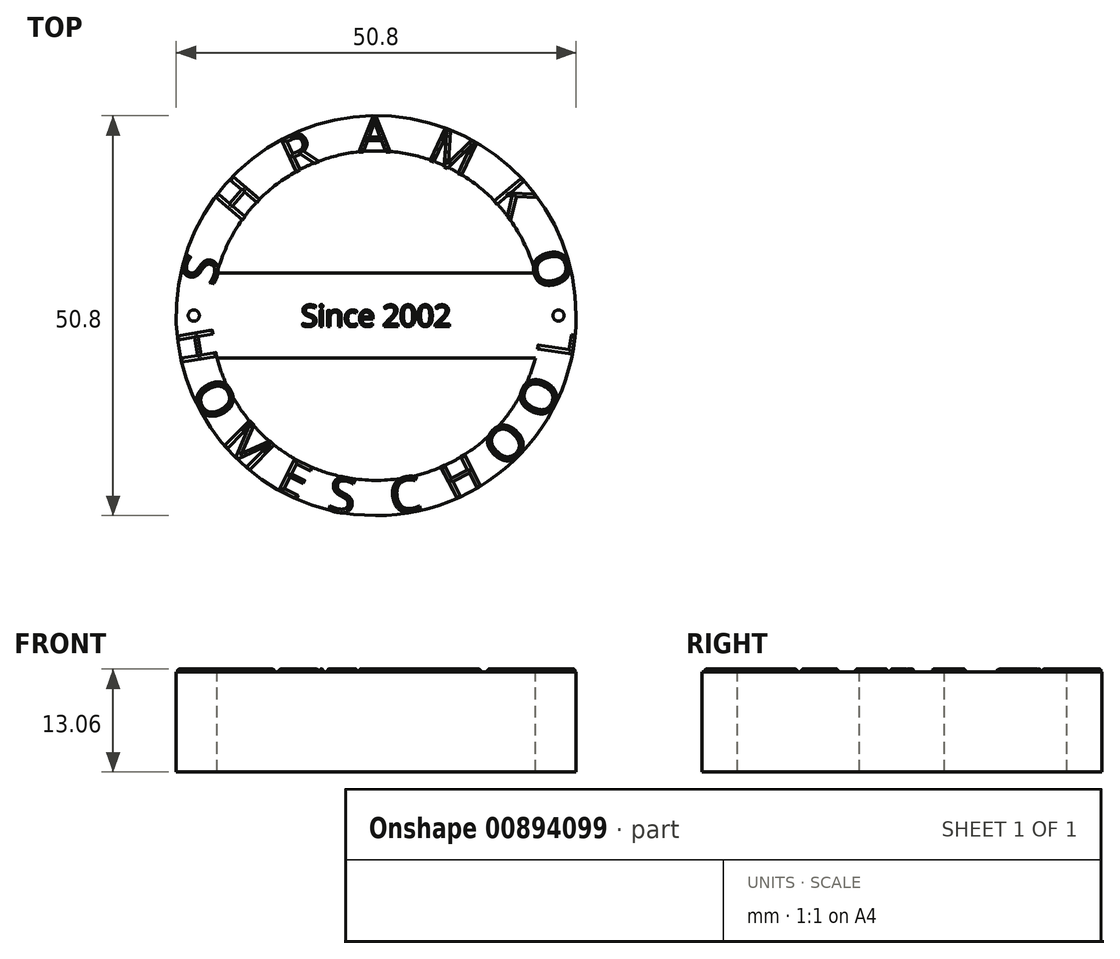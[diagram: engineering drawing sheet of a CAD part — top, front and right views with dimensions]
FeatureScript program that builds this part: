
annotation { "Feature Type Name" : "Feature", "Feature Type Description" : "" }
export const myFeature = defineFeature(function(context is Context, id is Id, definition is map)
    precondition{}
    {
        {
            var Q0;
            Q0=qCreatedBy(makeId("Top.planeOp"),FACE);
            var sketch = newSketch(context, id + "F0", { "sketchPlane" : qUnion([Q0])});
            skCircle(sketch, "E0", {"center": v(0, 0) * mm, "radius": 20.93 * mm, "construction": true});
            skCircle(sketch, "E1", {"center": v(0, 0) * mm, "radius": 25.4 * mm, "construction": true});
            skText(sketch, "E2", { "text": "S", "fontName": "OpenSans-Regular.ttf"});
            skText(sketch, "E3", { "text": "H", "fontName": "OpenSans-Regular.ttf"});
            skText(sketch, "E4", { "text": "R", "fontName": "OpenSans-Regular.ttf"});
            skText(sketch, "E5", { "text": "A", "fontName": "OpenSans-Regular.ttf"});
            skText(sketch, "E6", { "text": "M", "fontName": "OpenSans-Regular.ttf"});
            skText(sketch, "E7", { "text": "K", "fontName": "OpenSans-Regular.ttf"});
            skText(sketch, "E8", { "text": "O", "fontName": "OpenSans-Regular.ttf"});
            skCircle(sketch, "E9", {"center": v(-23.16, 0) * mm, "radius": 0.71 * mm});
            skCircle(sketch, "E10", {"center": v(23.16, 0) * mm, "radius": 0.71 * mm});
            skLineSegment(sketch, "E11", {"start": v(0, 0) * mm, "end": v(0, 25.3) * mm, "construction": true});
            skText(sketch, "E12", { "text": "H", "fontName": "OpenSans-Regular.ttf"});
            skText(sketch, "E13", { "text": "O", "fontName": "OpenSans-Regular.ttf"});
            skText(sketch, "E14", { "text": "M", "fontName": "OpenSans-Regular.ttf"});
            skText(sketch, "E15", { "text": "S", "fontName": "OpenSans-Regular.ttf"});
            skText(sketch, "E16", { "text": "C", "fontName": "OpenSans-Regular.ttf"});
            skText(sketch, "E17", { "text": "O", "fontName": "OpenSans-Regular.ttf"});
            skText(sketch, "E18", { "text": "O", "fontName": "OpenSans-Regular.ttf"});
            skText(sketch, "E19", { "text": "L", "fontName": "OpenSans-Regular.ttf"});
            skText(sketch, "E20", { "text": "E", "fontName": "OpenSans-Regular.ttf"});
            skText(sketch, "E21", { "text": "H", "fontName": "OpenSans-Regular.ttf"});
            const initialGuessF0  = {"E2": [-0.0206, 0.0037, 0.25882, 0.96593, 0.00448], "E3": [-0.01736, 0.0117, 0.64279, 0.76604, 0.0045], "E4": [-0.01068, 0.018, 0.9063, 0.42262, 0.00449], "E5": [-0.0022, 0.02078, 1, 0, 0.00452], "E6": [0.0063, 0.01996, 0.9063, -0.42262, 0.0045], "E7": [0.0146, 0.015, 0.64279, -0.76604, 0.00449], "E8": [0.02505, 0.00418, -0.25882, 0.96593, 0.0045], "E12": [-0.02532, -0.00198, 0.16413, -0.98644, 0.0045], "E13": [-0.02356, -0.00948, 0.46092, -0.88744, 0.0045], "E14": [-0.01966, -0.01609, 0.7126, -0.70157, 0.0045], "E15": [-0.0063, -0.02473, 0.98888, -0.14873, 0.00447], "E16": [0.0021, -0.02531, 0.98644, 0.16413, 0.00449], "E17": [0.0163, -0.01948, 0.70157, 0.7126, 0.0045], "E18": [0.02152, -0.01349, 0.44703, 0.89452, 0.0045], "E19": [0.0248, -0.0055, 0.14873, 0.98888, 0.00448], "E20": [-0.01289, -0.02189, 0.89452, -0.44703, 0.00448], "E21": [0.00971, -0.02347, 0.88744, 0.46092, 0.0045]};
            skSetInitialGuess(sketch, initialGuessF0);
            skSolve(sketch);
        }
        {
            var Q0;
            Q0 = qSketchRegion(id + "F0", true);
            extrude(context, id + "F1", {"entities" : qUnion([Q0]), "depth" : 0.36 * mm, "offsetDistance" : 25.4 * mm});
        }
        {
            var Q0;
            Q0=makeQuery(id+"F1.opExtrude","SWEPT_EDGE",EDGE,{"disambiguationData":[OSD([sQuery(id+"F0.wireOp",EDGE,"E14.sketch_text.stroke-16"),sQuery(id+"F0.wireOp",EDGE,"E14.sketch_text.stroke-17")])]});
            var Q1;
            Q1=makeQuery(id+"F1.opExtrude","SWEPT_EDGE",EDGE,{"disambiguationData":[OSD([sQuery(id+"F0.wireOp",EDGE,"E14.sketch_text.stroke-0"),sQuery(id+"F0.wireOp",EDGE,"E14.sketch_text.stroke-17")])]});
            var Q2;
            Q2=makeQuery(id+"F1.opExtrude","CAP_EDGE",EDGE,{"disambiguationData":[OSD([sQuery(id+"F0.wireOp",EDGE,"E14.sketch_text.stroke-16")])],"isStart":false});
            var Q3;
            Q3=makeQuery(id+"F1.opExtrude","CAP_EDGE",EDGE,{"disambiguationData":[OSD([sQuery(id+"F0.wireOp",EDGE,"E14.sketch_text.stroke-17")])],"isStart":false});
            var Q4;
            Q4=makeQuery(id+"F1.opExtrude","CAP_EDGE",EDGE,{"disambiguationData":[OSD([sQuery(id+"F0.wireOp",EDGE,"E14.sketch_text.stroke-12")])],"isStart":false});
            var Q5;
            Q5=makeQuery(id+"F1.opExtrude","CAP_EDGE",EDGE,{"disambiguationData":[OSD([sQuery(id+"F0.wireOp",EDGE,"E14.sketch_text.stroke-11")])],"isStart":false});
            var Q6;
            Q6=makeQuery(id+"F1.opExtrude","CAP_EDGE",EDGE,{"disambiguationData":[OSD([sQuery(id+"F0.wireOp",EDGE,"E14.sketch_text.stroke-13")])],"isStart":false});
            var Q7;
            Q7=makeQuery(id+"F1.opExtrude","CAP_EDGE",EDGE,{"disambiguationData":[OSD([sQuery(id+"F0.wireOp",EDGE,"E14.sketch_text.stroke-14")])],"isStart":false});
            var Q8;
            Q8=makeQuery(id+"F1.opExtrude","CAP_EDGE",EDGE,{"disambiguationData":[OSD([sQuery(id+"F0.wireOp",EDGE,"E14.sketch_text.stroke-10")])],"isStart":false});
            var Q9;
            Q9=makeQuery(id+"F1.opExtrude","CAP_EDGE",EDGE,{"disambiguationData":[OSD([sQuery(id+"F0.wireOp",EDGE,"E14.sketch_text.stroke-9")])],"isStart":false});
            var Q10;
            Q10=makeQuery(id+"F1.opExtrude","CAP_EDGE",EDGE,{"disambiguationData":[OSD([sQuery(id+"F0.wireOp",EDGE,"E14.sketch_text.stroke-7")])],"isStart":false});
            var Q11;
            Q11=makeQuery(id+"F1.opExtrude","CAP_EDGE",EDGE,{"disambiguationData":[OSD([sQuery(id+"F0.wireOp",EDGE,"E14.sketch_text.stroke-3")])],"isStart":false});
            var Q12;
            Q12=makeQuery(id+"F1.opExtrude","CAP_EDGE",EDGE,{"disambiguationData":[OSD([sQuery(id+"F0.wireOp",EDGE,"E14.sketch_text.stroke-5")])],"isStart":false});
            var Q13;
            Q13=makeQuery(id+"F1.opExtrude","CAP_EDGE",EDGE,{"disambiguationData":[OSD([sQuery(id+"F0.wireOp",EDGE,"E14.sketch_text.stroke-2")])],"isStart":false});
            var Q14;
            Q14=makeQuery(id+"F1.opExtrude","CAP_EDGE",EDGE,{"disambiguationData":[OSD([sQuery(id+"F0.wireOp",EDGE,"E14.sketch_text.stroke-6")])],"isStart":false});
            var Q15;
            Q15=makeQuery(id+"F1.opExtrude","CAP_EDGE",EDGE,{"disambiguationData":[OSD([sQuery(id+"F0.wireOp",EDGE,"E14.sketch_text.stroke-4")])],"isStart":false});
            var Q16;
            Q16=makeQuery(id+"F1.opExtrude","CAP_EDGE",EDGE,{"disambiguationData":[OSD([sQuery(id+"F0.wireOp",EDGE,"E20.sketch_text.stroke-2")])],"isStart":false});
            var Q17;
            Q17=makeQuery(id+"F1.opExtrude","CAP_EDGE",EDGE,{"disambiguationData":[OSD([sQuery(id+"F0.wireOp",EDGE,"E20.sketch_text.stroke-1")])],"isStart":false});
            var Q18;
            Q18=makeQuery(id+"F1.opExtrude","CAP_EDGE",EDGE,{"disambiguationData":[OSD([sQuery(id+"F0.wireOp",EDGE,"E20.sketch_text.stroke-5")])],"isStart":false});
            var Q19;
            Q19=makeQuery(id+"F1.opExtrude","CAP_EDGE",EDGE,{"disambiguationData":[OSD([sQuery(id+"F0.wireOp",EDGE,"E20.sketch_text.stroke-6")])],"isStart":false});
            var Q20;
            Q20=makeQuery(id+"F1.opExtrude","CAP_EDGE",EDGE,{"disambiguationData":[OSD([sQuery(id+"F0.wireOp",EDGE,"E20.sketch_text.stroke-8")])],"isStart":false});
            var Q21;
            Q21=makeQuery(id+"F1.opExtrude","CAP_EDGE",EDGE,{"disambiguationData":[OSD([sQuery(id+"F0.wireOp",EDGE,"E20.sketch_text.stroke-9")])],"isStart":false});
            var Q22;
            Q22=makeQuery(id+"F1.opExtrude","CAP_EDGE",EDGE,{"disambiguationData":[OSD([sQuery(id+"F0.wireOp",EDGE,"E20.sketch_text.stroke-0")])],"isStart":false});
            var Q23;
            Q23=makeQuery(id+"F1.opExtrude","CAP_EDGE",EDGE,{"disambiguationData":[OSD([sQuery(id+"F0.wireOp",EDGE,"E20.sketch_text.stroke-10")])],"isStart":false});
            var Q24;
            Q24=makeQuery(id+"F1.opExtrude","CAP_EDGE",EDGE,{"disambiguationData":[OSD([sQuery(id+"F0.wireOp",EDGE,"E20.sketch_text.stroke-11")])],"isStart":false});
            var Q25;
            Q25=makeQuery(id+"F1.opExtrude","CAP_EDGE",EDGE,{"disambiguationData":[OSD([sQuery(id+"F0.wireOp",EDGE,"E20.sketch_text.stroke-3")])],"isStart":false});
            var Q26;
            Q26=makeQuery(id+"F1.opExtrude","CAP_EDGE",EDGE,{"disambiguationData":[OSD([sQuery(id+"F0.wireOp",EDGE,"E20.sketch_text.stroke-7")])],"isStart":false});
            var Q27;
            Q27=makeQuery(id+"F1.opExtrude","CAP_EDGE",EDGE,{"disambiguationData":[OSD([sQuery(id+"F0.wireOp",EDGE,"E15.sketch_text.stroke-15")])],"isStart":false});
            var Q28;
            Q28=makeQuery(id+"F1.opExtrude","CAP_EDGE",EDGE,{"disambiguationData":[OSD([sQuery(id+"F0.wireOp",EDGE,"E15.sketch_text.stroke-14")])],"isStart":false});
            var Q29;
            Q29=makeQuery(id+"F1.opExtrude","CAP_EDGE",EDGE,{"disambiguationData":[OSD([sQuery(id+"F0.wireOp",EDGE,"E15.sketch_text.stroke-13")])],"isStart":false});
            var Q30;
            Q30=makeQuery(id+"F1.opExtrude","CAP_EDGE",EDGE,{"disambiguationData":[OSD([sQuery(id+"F0.wireOp",EDGE,"E15.sketch_text.stroke-12")])],"isStart":false});
            var Q31;
            Q31=makeQuery(id+"F1.opExtrude","CAP_EDGE",EDGE,{"disambiguationData":[OSD([sQuery(id+"F0.wireOp",EDGE,"E15.sketch_text.stroke-11")])],"isStart":false});
            var Q32;
            Q32=makeQuery(id+"F1.opExtrude","CAP_EDGE",EDGE,{"disambiguationData":[OSD([sQuery(id+"F0.wireOp",EDGE,"E15.sketch_text.stroke-10")])],"isStart":false});
            var Q33;
            Q33=makeQuery(id+"F1.opExtrude","CAP_EDGE",EDGE,{"disambiguationData":[OSD([sQuery(id+"F0.wireOp",EDGE,"E15.sketch_text.stroke-9")])],"isStart":false});
            var Q34;
            Q34=makeQuery(id+"F1.opExtrude","CAP_EDGE",EDGE,{"disambiguationData":[OSD([sQuery(id+"F0.wireOp",EDGE,"E15.sketch_text.stroke-8")])],"isStart":false});
            var Q35;
            Q35=makeQuery(id+"F1.opExtrude","CAP_EDGE",EDGE,{"disambiguationData":[OSD([sQuery(id+"F0.wireOp",EDGE,"E15.sketch_text.stroke-7")])],"isStart":false});
            var Q36;
            Q36=makeQuery(id+"F1.opExtrude","CAP_EDGE",EDGE,{"disambiguationData":[OSD([sQuery(id+"F0.wireOp",EDGE,"E15.sketch_text.stroke-6")])],"isStart":false});
            var Q37;
            Q37=makeQuery(id+"F1.opExtrude","CAP_EDGE",EDGE,{"disambiguationData":[OSD([sQuery(id+"F0.wireOp",EDGE,"E15.sketch_text.stroke-5")])],"isStart":false});
            var Q38;
            Q38=makeQuery(id+"F1.opExtrude","CAP_EDGE",EDGE,{"disambiguationData":[OSD([sQuery(id+"F0.wireOp",EDGE,"E15.sketch_text.stroke-4")])],"isStart":false});
            var Q39;
            Q39=makeQuery(id+"F1.opExtrude","CAP_EDGE",EDGE,{"disambiguationData":[OSD([sQuery(id+"F0.wireOp",EDGE,"E15.sketch_text.stroke-3")])],"isStart":false});
            var Q40;
            Q40=makeQuery(id+"F1.opExtrude","CAP_EDGE",EDGE,{"disambiguationData":[OSD([sQuery(id+"F0.wireOp",EDGE,"E15.sketch_text.stroke-2")])],"isStart":false});
            var Q41;
            Q41=makeQuery(id+"F1.opExtrude","CAP_EDGE",EDGE,{"disambiguationData":[OSD([sQuery(id+"F0.wireOp",EDGE,"E15.sketch_text.stroke-1")])],"isStart":false});
            var Q42;
            Q42=makeQuery(id+"F1.opExtrude","CAP_EDGE",EDGE,{"disambiguationData":[OSD([sQuery(id+"F0.wireOp",EDGE,"E15.sketch_text.stroke-0")])],"isStart":false});
            var Q43;
            Q43=makeQuery(id+"F1.opExtrude","CAP_EDGE",EDGE,{"disambiguationData":[OSD([sQuery(id+"F0.wireOp",EDGE,"E15.sketch_text.stroke-24")])],"isStart":false});
            var Q44;
            Q44=makeQuery(id+"F1.opExtrude","CAP_EDGE",EDGE,{"disambiguationData":[OSD([sQuery(id+"F0.wireOp",EDGE,"E15.sketch_text.stroke-23")])],"isStart":false});
            var Q45;
            Q45=makeQuery(id+"F1.opExtrude","CAP_EDGE",EDGE,{"disambiguationData":[OSD([sQuery(id+"F0.wireOp",EDGE,"E15.sketch_text.stroke-22")])],"isStart":false});
            var Q46;
            Q46=makeQuery(id+"F1.opExtrude","CAP_EDGE",EDGE,{"disambiguationData":[OSD([sQuery(id+"F0.wireOp",EDGE,"E15.sketch_text.stroke-20")])],"isStart":false});
            var Q47;
            Q47=makeQuery(id+"F1.opExtrude","CAP_EDGE",EDGE,{"disambiguationData":[OSD([sQuery(id+"F0.wireOp",EDGE,"E15.sketch_text.stroke-21")])],"isStart":false});
            var Q48;
            Q48=makeQuery(id+"F1.opExtrude","CAP_EDGE",EDGE,{"disambiguationData":[OSD([sQuery(id+"F0.wireOp",EDGE,"E15.sketch_text.stroke-19")])],"isStart":false});
            var Q49;
            Q49=makeQuery(id+"F1.opExtrude","CAP_EDGE",EDGE,{"disambiguationData":[OSD([sQuery(id+"F0.wireOp",EDGE,"E15.sketch_text.stroke-18")])],"isStart":false});
            var Q50;
            Q50=makeQuery(id+"F1.opExtrude","CAP_EDGE",EDGE,{"disambiguationData":[OSD([sQuery(id+"F0.wireOp",EDGE,"E15.sketch_text.stroke-17")])],"isStart":false});
            var Q51;
            Q51=makeQuery(id+"F1.opExtrude","CAP_EDGE",EDGE,{"disambiguationData":[OSD([sQuery(id+"F0.wireOp",EDGE,"E15.sketch_text.stroke-16")])],"isStart":false});
            var Q52;
            Q52=makeQuery(id+"F1.opExtrude","CAP_EDGE",EDGE,{"disambiguationData":[OSD([sQuery(id+"F0.wireOp",EDGE,"E16.sketch_text.stroke-13")])],"isStart":false});
            var Q53;
            Q53=makeQuery(id+"F1.opExtrude","CAP_EDGE",EDGE,{"disambiguationData":[OSD([sQuery(id+"F0.wireOp",EDGE,"E16.sketch_text.stroke-12")])],"isStart":false});
            var Q54;
            Q54=makeQuery(id+"F1.opExtrude","CAP_EDGE",EDGE,{"disambiguationData":[OSD([sQuery(id+"F0.wireOp",EDGE,"E16.sketch_text.stroke-11")])],"isStart":false});
            var Q55;
            Q55=makeQuery(id+"F1.opExtrude","CAP_EDGE",EDGE,{"disambiguationData":[OSD([sQuery(id+"F0.wireOp",EDGE,"E16.sketch_text.stroke-10")])],"isStart":false});
            var Q56;
            Q56=makeQuery(id+"F1.opExtrude","CAP_EDGE",EDGE,{"disambiguationData":[OSD([sQuery(id+"F0.wireOp",EDGE,"E16.sketch_text.stroke-9")])],"isStart":false});
            var Q57;
            Q57=makeQuery(id+"F1.opExtrude","CAP_EDGE",EDGE,{"disambiguationData":[OSD([sQuery(id+"F0.wireOp",EDGE,"E16.sketch_text.stroke-8")])],"isStart":false});
            var Q58;
            Q58=makeQuery(id+"F1.opExtrude","CAP_EDGE",EDGE,{"disambiguationData":[OSD([sQuery(id+"F0.wireOp",EDGE,"E16.sketch_text.stroke-7")])],"isStart":false});
            var Q59;
            Q59=makeQuery(id+"F1.opExtrude","CAP_EDGE",EDGE,{"disambiguationData":[OSD([sQuery(id+"F0.wireOp",EDGE,"E16.sketch_text.stroke-6")])],"isStart":false});
            var Q60;
            Q60=makeQuery(id+"F1.opExtrude","CAP_EDGE",EDGE,{"disambiguationData":[OSD([sQuery(id+"F0.wireOp",EDGE,"E16.sketch_text.stroke-5")])],"isStart":false});
            var Q61;
            Q61=makeQuery(id+"F1.opExtrude","CAP_EDGE",EDGE,{"disambiguationData":[OSD([sQuery(id+"F0.wireOp",EDGE,"E16.sketch_text.stroke-4")])],"isStart":false});
            var Q62;
            Q62=makeQuery(id+"F1.opExtrude","CAP_EDGE",EDGE,{"disambiguationData":[OSD([sQuery(id+"F0.wireOp",EDGE,"E16.sketch_text.stroke-3")])],"isStart":false});
            var Q63;
            Q63=makeQuery(id+"F1.opExtrude","CAP_EDGE",EDGE,{"disambiguationData":[OSD([sQuery(id+"F0.wireOp",EDGE,"E16.sketch_text.stroke-2")])],"isStart":false});
            var Q64;
            Q64=makeQuery(id+"F1.opExtrude","CAP_EDGE",EDGE,{"disambiguationData":[OSD([sQuery(id+"F0.wireOp",EDGE,"E16.sketch_text.stroke-1")])],"isStart":false});
            var Q65;
            Q65=makeQuery(id+"F1.opExtrude","CAP_EDGE",EDGE,{"disambiguationData":[OSD([sQuery(id+"F0.wireOp",EDGE,"E16.sketch_text.stroke-0")])],"isStart":false});
            var Q66;
            Q66=makeQuery(id+"F1.opExtrude","CAP_FACE",FACE,{"disambiguationData":[OSD([sQuery(id+"F0.wireOp",EDGE,"E16.sketch_text.stroke-0"),sQuery(id+"F0.wireOp",EDGE,"E16.sketch_text.stroke-1"),sQuery(id+"F0.wireOp",EDGE,"E16.sketch_text.stroke-2"),sQuery(id+"F0.wireOp",EDGE,"E16.sketch_text.stroke-3"),sQuery(id+"F0.wireOp",EDGE,"E16.sketch_text.stroke-4"),sQuery(id+"F0.wireOp",EDGE,"E16.sketch_text.stroke-5"),sQuery(id+"F0.wireOp",EDGE,"E16.sketch_text.stroke-6"),sQuery(id+"F0.wireOp",EDGE,"E16.sketch_text.stroke-7"),sQuery(id+"F0.wireOp",EDGE,"E16.sketch_text.stroke-8"),sQuery(id+"F0.wireOp",EDGE,"E16.sketch_text.stroke-9"),sQuery(id+"F0.wireOp",EDGE,"E16.sketch_text.stroke-10"),sQuery(id+"F0.wireOp",EDGE,"E16.sketch_text.stroke-11"),sQuery(id+"F0.wireOp",EDGE,"E16.sketch_text.stroke-12"),sQuery(id+"F0.wireOp",EDGE,"E16.sketch_text.stroke-13"),sQuery(id+"F0.wireOp",EDGE,"E16.sketch_text.stroke-14")])],"isStart":false});
            var Q67;
            Q67=makeQuery(id+"F1.opExtrude","CAP_EDGE",EDGE,{"disambiguationData":[OSD([sQuery(id+"F0.wireOp",EDGE,"E14.sketch_text.stroke-0")])],"isStart":false});
            var Q68;
            Q68=makeQuery(id+"F1.opExtrude","CAP_FACE",FACE,{"disambiguationData":[OSD([sQuery(id+"F0.wireOp",EDGE,"E14.sketch_text.stroke-0"),sQuery(id+"F0.wireOp",EDGE,"E14.sketch_text.stroke-1"),sQuery(id+"F0.wireOp",EDGE,"E14.sketch_text.stroke-2"),sQuery(id+"F0.wireOp",EDGE,"E14.sketch_text.stroke-3"),sQuery(id+"F0.wireOp",EDGE,"E14.sketch_text.stroke-4"),sQuery(id+"F0.wireOp",EDGE,"E14.sketch_text.stroke-5"),sQuery(id+"F0.wireOp",EDGE,"E14.sketch_text.stroke-6"),sQuery(id+"F0.wireOp",EDGE,"E14.sketch_text.stroke-7"),sQuery(id+"F0.wireOp",EDGE,"E14.sketch_text.stroke-8"),sQuery(id+"F0.wireOp",EDGE,"E14.sketch_text.stroke-9"),sQuery(id+"F0.wireOp",EDGE,"E14.sketch_text.stroke-10"),sQuery(id+"F0.wireOp",EDGE,"E14.sketch_text.stroke-11"),sQuery(id+"F0.wireOp",EDGE,"E14.sketch_text.stroke-12"),sQuery(id+"F0.wireOp",EDGE,"E14.sketch_text.stroke-13"),sQuery(id+"F0.wireOp",EDGE,"E14.sketch_text.stroke-14"),sQuery(id+"F0.wireOp",EDGE,"E14.sketch_text.stroke-15"),sQuery(id+"F0.wireOp",EDGE,"E14.sketch_text.stroke-16"),sQuery(id+"F0.wireOp",EDGE,"E14.sketch_text.stroke-17")])],"isStart":false});
            var Q69;
            Q69=makeQuery(id+"F1.opExtrude","CAP_EDGE",EDGE,{"disambiguationData":[OSD([sQuery(id+"F0.wireOp",EDGE,"E20.sketch_text.stroke-4")])],"isStart":false});
            var Q70;
            Q70=makeQuery(id+"F1.opExtrude","CAP_EDGE",EDGE,{"disambiguationData":[OSD([sQuery(id+"F0.wireOp",EDGE,"E17.sketch_text.stroke-3")])],"isStart":false});
            var Q71;
            Q71=makeQuery(id+"F1.opExtrude","CAP_EDGE",EDGE,{"disambiguationData":[OSD([sQuery(id+"F0.wireOp",EDGE,"E17.sketch_text.stroke-11")])],"isStart":false});
            var Q72;
            Q72=makeQuery(id+"F1.opExtrude","CAP_EDGE",EDGE,{"disambiguationData":[OSD([sQuery(id+"F0.wireOp",EDGE,"E17.sketch_text.stroke-12")])],"isStart":false});
            var Q73;
            Q73=makeQuery(id+"F1.opExtrude","CAP_FACE",FACE,{"disambiguationData":[OSD([sQuery(id+"F0.wireOp",EDGE,"E18.sketch_text.stroke-0"),sQuery(id+"F0.wireOp",EDGE,"E18.sketch_text.stroke-1"),sQuery(id+"F0.wireOp",EDGE,"E18.sketch_text.stroke-2"),sQuery(id+"F0.wireOp",EDGE,"E18.sketch_text.stroke-3"),sQuery(id+"F0.wireOp",EDGE,"E18.sketch_text.stroke-4"),sQuery(id+"F0.wireOp",EDGE,"E18.sketch_text.stroke-5"),sQuery(id+"F0.wireOp",EDGE,"E18.sketch_text.stroke-6"),sQuery(id+"F0.wireOp",EDGE,"E18.sketch_text.stroke-7"),sQuery(id+"F0.wireOp",EDGE,"E18.sketch_text.stroke-8"),sQuery(id+"F0.wireOp",EDGE,"E18.sketch_text.stroke-9"),sQuery(id+"F0.wireOp",EDGE,"E18.sketch_text.stroke-10"),sQuery(id+"F0.wireOp",EDGE,"E18.sketch_text.stroke-11"),sQuery(id+"F0.wireOp",EDGE,"E18.sketch_text.stroke-12"),sQuery(id+"F0.wireOp",EDGE,"E18.sketch_text.stroke-13"),sQuery(id+"F0.wireOp",EDGE,"E18.sketch_text.stroke-14"),sQuery(id+"F0.wireOp",EDGE,"E18.sketch_text.stroke-15")])],"isStart":false});
            var Q74;
            Q74=makeQuery(id+"F1.opExtrude","CAP_FACE",FACE,{"disambiguationData":[OSD([sQuery(id+"F0.wireOp",EDGE,"E19.sketch_text.stroke-0"),sQuery(id+"F0.wireOp",EDGE,"E19.sketch_text.stroke-1"),sQuery(id+"F0.wireOp",EDGE,"E19.sketch_text.stroke-2"),sQuery(id+"F0.wireOp",EDGE,"E19.sketch_text.stroke-3"),sQuery(id+"F0.wireOp",EDGE,"E19.sketch_text.stroke-4"),sQuery(id+"F0.wireOp",EDGE,"E19.sketch_text.stroke-5")])],"isStart":false});
            var Q75;
            Q75=makeQuery(id+"F1.opExtrude","CAP_FACE",FACE,{"disambiguationData":[OSD([sQuery(id+"F0.wireOp",EDGE,"E10")])],"isStart":false});
            var Q76;
            Q76=makeQuery(id+"F1.opExtrude","CAP_FACE",FACE,{"disambiguationData":[OSD([sQuery(id+"F0.wireOp",EDGE,"E8.sketch_text.stroke-0"),sQuery(id+"F0.wireOp",EDGE,"E8.sketch_text.stroke-1"),sQuery(id+"F0.wireOp",EDGE,"E8.sketch_text.stroke-2"),sQuery(id+"F0.wireOp",EDGE,"E8.sketch_text.stroke-3"),sQuery(id+"F0.wireOp",EDGE,"E8.sketch_text.stroke-4"),sQuery(id+"F0.wireOp",EDGE,"E8.sketch_text.stroke-5"),sQuery(id+"F0.wireOp",EDGE,"E8.sketch_text.stroke-6"),sQuery(id+"F0.wireOp",EDGE,"E8.sketch_text.stroke-7"),sQuery(id+"F0.wireOp",EDGE,"E8.sketch_text.stroke-8"),sQuery(id+"F0.wireOp",EDGE,"E8.sketch_text.stroke-9"),sQuery(id+"F0.wireOp",EDGE,"E8.sketch_text.stroke-10"),sQuery(id+"F0.wireOp",EDGE,"E8.sketch_text.stroke-11"),sQuery(id+"F0.wireOp",EDGE,"E8.sketch_text.stroke-12"),sQuery(id+"F0.wireOp",EDGE,"E8.sketch_text.stroke-13"),sQuery(id+"F0.wireOp",EDGE,"E8.sketch_text.stroke-14"),sQuery(id+"F0.wireOp",EDGE,"E8.sketch_text.stroke-15")])],"isStart":false});
            var Q77;
            Q77=makeQuery(id+"F1.opExtrude","CAP_FACE",FACE,{"disambiguationData":[OSD([sQuery(id+"F0.wireOp",EDGE,"E7.sketch_text.stroke-0"),sQuery(id+"F0.wireOp",EDGE,"E7.sketch_text.stroke-1"),sQuery(id+"F0.wireOp",EDGE,"E7.sketch_text.stroke-2"),sQuery(id+"F0.wireOp",EDGE,"E7.sketch_text.stroke-3"),sQuery(id+"F0.wireOp",EDGE,"E7.sketch_text.stroke-4"),sQuery(id+"F0.wireOp",EDGE,"E7.sketch_text.stroke-5"),sQuery(id+"F0.wireOp",EDGE,"E7.sketch_text.stroke-6"),sQuery(id+"F0.wireOp",EDGE,"E7.sketch_text.stroke-7"),sQuery(id+"F0.wireOp",EDGE,"E7.sketch_text.stroke-8"),sQuery(id+"F0.wireOp",EDGE,"E7.sketch_text.stroke-9"),sQuery(id+"F0.wireOp",EDGE,"E7.sketch_text.stroke-10"),sQuery(id+"F0.wireOp",EDGE,"E7.sketch_text.stroke-11")])],"isStart":false});
            var Q78;
            Q78=makeQuery(id+"F1.opExtrude","CAP_FACE",FACE,{"disambiguationData":[OSD([sQuery(id+"F0.wireOp",EDGE,"E6.sketch_text.stroke-0"),sQuery(id+"F0.wireOp",EDGE,"E6.sketch_text.stroke-1"),sQuery(id+"F0.wireOp",EDGE,"E6.sketch_text.stroke-2"),sQuery(id+"F0.wireOp",EDGE,"E6.sketch_text.stroke-3"),sQuery(id+"F0.wireOp",EDGE,"E6.sketch_text.stroke-4"),sQuery(id+"F0.wireOp",EDGE,"E6.sketch_text.stroke-5"),sQuery(id+"F0.wireOp",EDGE,"E6.sketch_text.stroke-6"),sQuery(id+"F0.wireOp",EDGE,"E6.sketch_text.stroke-7"),sQuery(id+"F0.wireOp",EDGE,"E6.sketch_text.stroke-8"),sQuery(id+"F0.wireOp",EDGE,"E6.sketch_text.stroke-9"),sQuery(id+"F0.wireOp",EDGE,"E6.sketch_text.stroke-10"),sQuery(id+"F0.wireOp",EDGE,"E6.sketch_text.stroke-11"),sQuery(id+"F0.wireOp",EDGE,"E6.sketch_text.stroke-12"),sQuery(id+"F0.wireOp",EDGE,"E6.sketch_text.stroke-13"),sQuery(id+"F0.wireOp",EDGE,"E6.sketch_text.stroke-14"),sQuery(id+"F0.wireOp",EDGE,"E6.sketch_text.stroke-15"),sQuery(id+"F0.wireOp",EDGE,"E6.sketch_text.stroke-16"),sQuery(id+"F0.wireOp",EDGE,"E6.sketch_text.stroke-17")])],"isStart":false});
            var Q79;
            Q79=makeQuery(id+"F1.opExtrude","CAP_FACE",FACE,{"disambiguationData":[OSD([sQuery(id+"F0.wireOp",EDGE,"E5.sketch_text.stroke-0"),sQuery(id+"F0.wireOp",EDGE,"E5.sketch_text.stroke-1"),sQuery(id+"F0.wireOp",EDGE,"E5.sketch_text.stroke-2"),sQuery(id+"F0.wireOp",EDGE,"E5.sketch_text.stroke-3"),sQuery(id+"F0.wireOp",EDGE,"E5.sketch_text.stroke-4"),sQuery(id+"F0.wireOp",EDGE,"E5.sketch_text.stroke-5"),sQuery(id+"F0.wireOp",EDGE,"E5.sketch_text.stroke-6"),sQuery(id+"F0.wireOp",EDGE,"E5.sketch_text.stroke-7"),sQuery(id+"F0.wireOp",EDGE,"E5.sketch_text.stroke-8"),sQuery(id+"F0.wireOp",EDGE,"E5.sketch_text.stroke-9"),sQuery(id+"F0.wireOp",EDGE,"E5.sketch_text.stroke-10"),sQuery(id+"F0.wireOp",EDGE,"E5.sketch_text.stroke-11"),sQuery(id+"F0.wireOp",EDGE,"E5.sketch_text.stroke-12")])],"isStart":false});
            var Q80;
            Q80=makeQuery(id+"F1.opExtrude","CAP_FACE",FACE,{"disambiguationData":[OSD([sQuery(id+"F0.wireOp",EDGE,"E4.sketch_text.stroke-0"),sQuery(id+"F0.wireOp",EDGE,"E4.sketch_text.stroke-1"),sQuery(id+"F0.wireOp",EDGE,"E4.sketch_text.stroke-2"),sQuery(id+"F0.wireOp",EDGE,"E4.sketch_text.stroke-3"),sQuery(id+"F0.wireOp",EDGE,"E4.sketch_text.stroke-4"),sQuery(id+"F0.wireOp",EDGE,"E4.sketch_text.stroke-5"),sQuery(id+"F0.wireOp",EDGE,"E4.sketch_text.stroke-6"),sQuery(id+"F0.wireOp",EDGE,"E4.sketch_text.stroke-7"),sQuery(id+"F0.wireOp",EDGE,"E4.sketch_text.stroke-8"),sQuery(id+"F0.wireOp",EDGE,"E4.sketch_text.stroke-9"),sQuery(id+"F0.wireOp",EDGE,"E4.sketch_text.stroke-10"),sQuery(id+"F0.wireOp",EDGE,"E4.sketch_text.stroke-11"),sQuery(id+"F0.wireOp",EDGE,"E4.sketch_text.stroke-12"),sQuery(id+"F0.wireOp",EDGE,"E4.sketch_text.stroke-13"),sQuery(id+"F0.wireOp",EDGE,"E4.sketch_text.stroke-14"),sQuery(id+"F0.wireOp",EDGE,"E4.sketch_text.stroke-15"),sQuery(id+"F0.wireOp",EDGE,"E4.sketch_text.stroke-16"),sQuery(id+"F0.wireOp",EDGE,"E4.sketch_text.stroke-17")])],"isStart":false});
            var Q81;
            Q81=makeQuery(id+"F1.opExtrude","CAP_FACE",FACE,{"disambiguationData":[OSD([sQuery(id+"F0.wireOp",EDGE,"E3.sketch_text.stroke-0"),sQuery(id+"F0.wireOp",EDGE,"E3.sketch_text.stroke-1"),sQuery(id+"F0.wireOp",EDGE,"E3.sketch_text.stroke-2"),sQuery(id+"F0.wireOp",EDGE,"E3.sketch_text.stroke-3"),sQuery(id+"F0.wireOp",EDGE,"E3.sketch_text.stroke-4"),sQuery(id+"F0.wireOp",EDGE,"E3.sketch_text.stroke-5"),sQuery(id+"F0.wireOp",EDGE,"E3.sketch_text.stroke-6"),sQuery(id+"F0.wireOp",EDGE,"E3.sketch_text.stroke-7"),sQuery(id+"F0.wireOp",EDGE,"E3.sketch_text.stroke-8"),sQuery(id+"F0.wireOp",EDGE,"E3.sketch_text.stroke-9"),sQuery(id+"F0.wireOp",EDGE,"E3.sketch_text.stroke-10"),sQuery(id+"F0.wireOp",EDGE,"E3.sketch_text.stroke-11")])],"isStart":false});
            var Q82;
            Q82=makeQuery(id+"F1.opExtrude","CAP_FACE",FACE,{"disambiguationData":[OSD([sQuery(id+"F0.wireOp",EDGE,"E2.sketch_text.stroke-0"),sQuery(id+"F0.wireOp",EDGE,"E2.sketch_text.stroke-1"),sQuery(id+"F0.wireOp",EDGE,"E2.sketch_text.stroke-2"),sQuery(id+"F0.wireOp",EDGE,"E2.sketch_text.stroke-3"),sQuery(id+"F0.wireOp",EDGE,"E2.sketch_text.stroke-4"),sQuery(id+"F0.wireOp",EDGE,"E2.sketch_text.stroke-5"),sQuery(id+"F0.wireOp",EDGE,"E2.sketch_text.stroke-6"),sQuery(id+"F0.wireOp",EDGE,"E2.sketch_text.stroke-7"),sQuery(id+"F0.wireOp",EDGE,"E2.sketch_text.stroke-8"),sQuery(id+"F0.wireOp",EDGE,"E2.sketch_text.stroke-9"),sQuery(id+"F0.wireOp",EDGE,"E2.sketch_text.stroke-10"),sQuery(id+"F0.wireOp",EDGE,"E2.sketch_text.stroke-11"),sQuery(id+"F0.wireOp",EDGE,"E2.sketch_text.stroke-12"),sQuery(id+"F0.wireOp",EDGE,"E2.sketch_text.stroke-13"),sQuery(id+"F0.wireOp",EDGE,"E2.sketch_text.stroke-14"),sQuery(id+"F0.wireOp",EDGE,"E2.sketch_text.stroke-15"),sQuery(id+"F0.wireOp",EDGE,"E2.sketch_text.stroke-16"),sQuery(id+"F0.wireOp",EDGE,"E2.sketch_text.stroke-17"),sQuery(id+"F0.wireOp",EDGE,"E2.sketch_text.stroke-18"),sQuery(id+"F0.wireOp",EDGE,"E2.sketch_text.stroke-19"),sQuery(id+"F0.wireOp",EDGE,"E2.sketch_text.stroke-20"),sQuery(id+"F0.wireOp",EDGE,"E2.sketch_text.stroke-21"),sQuery(id+"F0.wireOp",EDGE,"E2.sketch_text.stroke-22"),sQuery(id+"F0.wireOp",EDGE,"E2.sketch_text.stroke-23"),sQuery(id+"F0.wireOp",EDGE,"E2.sketch_text.stroke-24")])],"isStart":false});
            var Q83;
            Q83=makeQuery(id+"F1.opExtrude","CAP_FACE",FACE,{"disambiguationData":[OSD([sQuery(id+"F0.wireOp",EDGE,"E9")])],"isStart":false});
            var Q84;
            Q84=makeQuery(id+"F1.opExtrude","CAP_FACE",FACE,{"disambiguationData":[OSD([sQuery(id+"F0.wireOp",EDGE,"E12.sketch_text.stroke-0"),sQuery(id+"F0.wireOp",EDGE,"E12.sketch_text.stroke-1"),sQuery(id+"F0.wireOp",EDGE,"E12.sketch_text.stroke-2"),sQuery(id+"F0.wireOp",EDGE,"E12.sketch_text.stroke-3"),sQuery(id+"F0.wireOp",EDGE,"E12.sketch_text.stroke-4"),sQuery(id+"F0.wireOp",EDGE,"E12.sketch_text.stroke-5"),sQuery(id+"F0.wireOp",EDGE,"E12.sketch_text.stroke-6"),sQuery(id+"F0.wireOp",EDGE,"E12.sketch_text.stroke-7"),sQuery(id+"F0.wireOp",EDGE,"E12.sketch_text.stroke-8"),sQuery(id+"F0.wireOp",EDGE,"E12.sketch_text.stroke-9"),sQuery(id+"F0.wireOp",EDGE,"E12.sketch_text.stroke-10"),sQuery(id+"F0.wireOp",EDGE,"E12.sketch_text.stroke-11")])],"isStart":false});
            var Q85;
            Q85=makeQuery(id+"F1.opExtrude","CAP_FACE",FACE,{"disambiguationData":[OSD([sQuery(id+"F0.wireOp",EDGE,"E13.sketch_text.stroke-0"),sQuery(id+"F0.wireOp",EDGE,"E13.sketch_text.stroke-1"),sQuery(id+"F0.wireOp",EDGE,"E13.sketch_text.stroke-2"),sQuery(id+"F0.wireOp",EDGE,"E13.sketch_text.stroke-3"),sQuery(id+"F0.wireOp",EDGE,"E13.sketch_text.stroke-4"),sQuery(id+"F0.wireOp",EDGE,"E13.sketch_text.stroke-5"),sQuery(id+"F0.wireOp",EDGE,"E13.sketch_text.stroke-6"),sQuery(id+"F0.wireOp",EDGE,"E13.sketch_text.stroke-7"),sQuery(id+"F0.wireOp",EDGE,"E13.sketch_text.stroke-8"),sQuery(id+"F0.wireOp",EDGE,"E13.sketch_text.stroke-9"),sQuery(id+"F0.wireOp",EDGE,"E13.sketch_text.stroke-10"),sQuery(id+"F0.wireOp",EDGE,"E13.sketch_text.stroke-11"),sQuery(id+"F0.wireOp",EDGE,"E13.sketch_text.stroke-12"),sQuery(id+"F0.wireOp",EDGE,"E13.sketch_text.stroke-13"),sQuery(id+"F0.wireOp",EDGE,"E13.sketch_text.stroke-14"),sQuery(id+"F0.wireOp",EDGE,"E13.sketch_text.stroke-15")])],"isStart":false});
            var Q86;
            Q86=makeQuery(id+"F1.opExtrude","CAP_FACE",FACE,{"disambiguationData":[OSD([sQuery(id+"F0.wireOp",EDGE,"E21.sketch_text.stroke-0"),sQuery(id+"F0.wireOp",EDGE,"E21.sketch_text.stroke-1"),sQuery(id+"F0.wireOp",EDGE,"E21.sketch_text.stroke-2"),sQuery(id+"F0.wireOp",EDGE,"E21.sketch_text.stroke-3"),sQuery(id+"F0.wireOp",EDGE,"E21.sketch_text.stroke-4"),sQuery(id+"F0.wireOp",EDGE,"E21.sketch_text.stroke-5"),sQuery(id+"F0.wireOp",EDGE,"E21.sketch_text.stroke-6"),sQuery(id+"F0.wireOp",EDGE,"E21.sketch_text.stroke-7"),sQuery(id+"F0.wireOp",EDGE,"E21.sketch_text.stroke-8"),sQuery(id+"F0.wireOp",EDGE,"E21.sketch_text.stroke-9"),sQuery(id+"F0.wireOp",EDGE,"E21.sketch_text.stroke-10"),sQuery(id+"F0.wireOp",EDGE,"E21.sketch_text.stroke-11")])],"isStart":false});
            fillet(context, id + "F2", {"entities" : qUnion([Q0, Q1, Q2, Q3, Q4, Q5, Q6, Q7, Q8, Q9, Q10, Q11, Q12, Q13, Q14, Q15, Q16, Q17, Q18, Q19, Q20, Q21, Q22, Q23, Q24, Q25, Q26, Q27, Q28, Q29, Q30, Q31, Q32, Q33, Q34, Q35, Q36, Q37, Q38, Q39, Q40, Q41, Q42, Q43, Q44, Q45, Q46, Q47, Q48, Q49, Q50, Q51, Q52, Q53, Q54, Q55, Q56, Q57, Q58, Q59, Q60, Q61, Q62, Q63, Q64, Q65, Q66, Q67, Q68, Q69, Q70, Q71, Q72, Q73, Q74, Q75, Q76, Q77, Q78, Q79, Q80, Q81, Q82, Q83, Q84, Q85, Q86]), "radius" : 0.2 * mm, "tangentPropagation" : true, "allowEdgeOverflow" : false});
        }
        {
            var Q0;
            Q0=qCreatedBy(makeId("Top.planeOp"),FACE);
            var sketch = newSketch(context, id + "F3", { "sketchPlane" : qUnion([Q0])});
            skCircle(sketch, "E22", {"center": v(0, 0) * mm, "radius": 25.4 * mm});
            skCircle(sketch, "E23", {"center": v(0, 0) * mm, "radius": 20.93 * mm});
            skSolve(sketch);
        }
        {
            var Q0;
            Q0 = qSketchRegion(id + "F3", true);
            extrude(context, id + "F4", {"entities" : qUnion([Q0]), "oppositeDirection" : true, "depth" : 12.7 * mm, "offsetDistance" : 25.4 * mm});
        }
        {
            var Q0;
            Q0=makeQuery(id+"F1.opExtrude","SWEPT_BODY",BODY,{"disambiguationData":[OSD([sQuery(id+"F0.wireOp",EDGE,"E2.sketch_text.stroke-0"),sQuery(id+"F0.wireOp",EDGE,"E2.sketch_text.stroke-1"),sQuery(id+"F0.wireOp",EDGE,"E2.sketch_text.stroke-2"),sQuery(id+"F0.wireOp",EDGE,"E2.sketch_text.stroke-3"),sQuery(id+"F0.wireOp",EDGE,"E2.sketch_text.stroke-4"),sQuery(id+"F0.wireOp",EDGE,"E2.sketch_text.stroke-5"),sQuery(id+"F0.wireOp",EDGE,"E2.sketch_text.stroke-6"),sQuery(id+"F0.wireOp",EDGE,"E2.sketch_text.stroke-7"),sQuery(id+"F0.wireOp",EDGE,"E2.sketch_text.stroke-8"),sQuery(id+"F0.wireOp",EDGE,"E2.sketch_text.stroke-9"),sQuery(id+"F0.wireOp",EDGE,"E2.sketch_text.stroke-10"),sQuery(id+"F0.wireOp",EDGE,"E2.sketch_text.stroke-11"),sQuery(id+"F0.wireOp",EDGE,"E2.sketch_text.stroke-12"),sQuery(id+"F0.wireOp",EDGE,"E2.sketch_text.stroke-13"),sQuery(id+"F0.wireOp",EDGE,"E2.sketch_text.stroke-14"),sQuery(id+"F0.wireOp",EDGE,"E2.sketch_text.stroke-15"),sQuery(id+"F0.wireOp",EDGE,"E2.sketch_text.stroke-16"),sQuery(id+"F0.wireOp",EDGE,"E2.sketch_text.stroke-17"),sQuery(id+"F0.wireOp",EDGE,"E2.sketch_text.stroke-18"),sQuery(id+"F0.wireOp",EDGE,"E2.sketch_text.stroke-19"),sQuery(id+"F0.wireOp",EDGE,"E2.sketch_text.stroke-20"),sQuery(id+"F0.wireOp",EDGE,"E2.sketch_text.stroke-21"),sQuery(id+"F0.wireOp",EDGE,"E2.sketch_text.stroke-22"),sQuery(id+"F0.wireOp",EDGE,"E2.sketch_text.stroke-23"),sQuery(id+"F0.wireOp",EDGE,"E2.sketch_text.stroke-24")])]});
            var Q1;
            Q1=makeQuery(id+"F1.opExtrude","SWEPT_BODY",BODY,{"disambiguationData":[OSD([sQuery(id+"F0.wireOp",EDGE,"E3.sketch_text.stroke-0"),sQuery(id+"F0.wireOp",EDGE,"E3.sketch_text.stroke-1"),sQuery(id+"F0.wireOp",EDGE,"E3.sketch_text.stroke-2"),sQuery(id+"F0.wireOp",EDGE,"E3.sketch_text.stroke-3"),sQuery(id+"F0.wireOp",EDGE,"E3.sketch_text.stroke-4"),sQuery(id+"F0.wireOp",EDGE,"E3.sketch_text.stroke-5"),sQuery(id+"F0.wireOp",EDGE,"E3.sketch_text.stroke-6"),sQuery(id+"F0.wireOp",EDGE,"E3.sketch_text.stroke-7"),sQuery(id+"F0.wireOp",EDGE,"E3.sketch_text.stroke-8"),sQuery(id+"F0.wireOp",EDGE,"E3.sketch_text.stroke-9"),sQuery(id+"F0.wireOp",EDGE,"E3.sketch_text.stroke-10"),sQuery(id+"F0.wireOp",EDGE,"E3.sketch_text.stroke-11")])]});
            var Q2;
            Q2=makeQuery(id+"F1.opExtrude","SWEPT_BODY",BODY,{"disambiguationData":[OSD([sQuery(id+"F0.wireOp",EDGE,"E4.sketch_text.stroke-0"),sQuery(id+"F0.wireOp",EDGE,"E4.sketch_text.stroke-1"),sQuery(id+"F0.wireOp",EDGE,"E4.sketch_text.stroke-2"),sQuery(id+"F0.wireOp",EDGE,"E4.sketch_text.stroke-3"),sQuery(id+"F0.wireOp",EDGE,"E4.sketch_text.stroke-4"),sQuery(id+"F0.wireOp",EDGE,"E4.sketch_text.stroke-5"),sQuery(id+"F0.wireOp",EDGE,"E4.sketch_text.stroke-6"),sQuery(id+"F0.wireOp",EDGE,"E4.sketch_text.stroke-7"),sQuery(id+"F0.wireOp",EDGE,"E4.sketch_text.stroke-8"),sQuery(id+"F0.wireOp",EDGE,"E4.sketch_text.stroke-9"),sQuery(id+"F0.wireOp",EDGE,"E4.sketch_text.stroke-10"),sQuery(id+"F0.wireOp",EDGE,"E4.sketch_text.stroke-11"),sQuery(id+"F0.wireOp",EDGE,"E4.sketch_text.stroke-12"),sQuery(id+"F0.wireOp",EDGE,"E4.sketch_text.stroke-13"),sQuery(id+"F0.wireOp",EDGE,"E4.sketch_text.stroke-14"),sQuery(id+"F0.wireOp",EDGE,"E4.sketch_text.stroke-15"),sQuery(id+"F0.wireOp",EDGE,"E4.sketch_text.stroke-16"),sQuery(id+"F0.wireOp",EDGE,"E4.sketch_text.stroke-17")])]});
            var Q3;
            Q3=makeQuery(id+"F1.opExtrude","SWEPT_BODY",BODY,{"disambiguationData":[OSD([sQuery(id+"F0.wireOp",EDGE,"E5.sketch_text.stroke-0"),sQuery(id+"F0.wireOp",EDGE,"E5.sketch_text.stroke-1"),sQuery(id+"F0.wireOp",EDGE,"E5.sketch_text.stroke-2"),sQuery(id+"F0.wireOp",EDGE,"E5.sketch_text.stroke-3"),sQuery(id+"F0.wireOp",EDGE,"E5.sketch_text.stroke-4"),sQuery(id+"F0.wireOp",EDGE,"E5.sketch_text.stroke-5"),sQuery(id+"F0.wireOp",EDGE,"E5.sketch_text.stroke-6"),sQuery(id+"F0.wireOp",EDGE,"E5.sketch_text.stroke-7"),sQuery(id+"F0.wireOp",EDGE,"E5.sketch_text.stroke-8"),sQuery(id+"F0.wireOp",EDGE,"E5.sketch_text.stroke-9"),sQuery(id+"F0.wireOp",EDGE,"E5.sketch_text.stroke-10"),sQuery(id+"F0.wireOp",EDGE,"E5.sketch_text.stroke-11"),sQuery(id+"F0.wireOp",EDGE,"E5.sketch_text.stroke-12")])]});
            var Q4;
            Q4=makeQuery(id+"F1.opExtrude","SWEPT_BODY",BODY,{"disambiguationData":[OSD([sQuery(id+"F0.wireOp",EDGE,"E6.sketch_text.stroke-0"),sQuery(id+"F0.wireOp",EDGE,"E6.sketch_text.stroke-1"),sQuery(id+"F0.wireOp",EDGE,"E6.sketch_text.stroke-2"),sQuery(id+"F0.wireOp",EDGE,"E6.sketch_text.stroke-3"),sQuery(id+"F0.wireOp",EDGE,"E6.sketch_text.stroke-4"),sQuery(id+"F0.wireOp",EDGE,"E6.sketch_text.stroke-5"),sQuery(id+"F0.wireOp",EDGE,"E6.sketch_text.stroke-6"),sQuery(id+"F0.wireOp",EDGE,"E6.sketch_text.stroke-7"),sQuery(id+"F0.wireOp",EDGE,"E6.sketch_text.stroke-8"),sQuery(id+"F0.wireOp",EDGE,"E6.sketch_text.stroke-9"),sQuery(id+"F0.wireOp",EDGE,"E6.sketch_text.stroke-10"),sQuery(id+"F0.wireOp",EDGE,"E6.sketch_text.stroke-11"),sQuery(id+"F0.wireOp",EDGE,"E6.sketch_text.stroke-12"),sQuery(id+"F0.wireOp",EDGE,"E6.sketch_text.stroke-13"),sQuery(id+"F0.wireOp",EDGE,"E6.sketch_text.stroke-14"),sQuery(id+"F0.wireOp",EDGE,"E6.sketch_text.stroke-15"),sQuery(id+"F0.wireOp",EDGE,"E6.sketch_text.stroke-16"),sQuery(id+"F0.wireOp",EDGE,"E6.sketch_text.stroke-17")])]});
            var Q5;
            Q5=makeQuery(id+"F1.opExtrude","SWEPT_BODY",BODY,{"disambiguationData":[OSD([sQuery(id+"F0.wireOp",EDGE,"E7.sketch_text.stroke-0"),sQuery(id+"F0.wireOp",EDGE,"E7.sketch_text.stroke-1"),sQuery(id+"F0.wireOp",EDGE,"E7.sketch_text.stroke-2"),sQuery(id+"F0.wireOp",EDGE,"E7.sketch_text.stroke-3"),sQuery(id+"F0.wireOp",EDGE,"E7.sketch_text.stroke-4"),sQuery(id+"F0.wireOp",EDGE,"E7.sketch_text.stroke-5"),sQuery(id+"F0.wireOp",EDGE,"E7.sketch_text.stroke-6"),sQuery(id+"F0.wireOp",EDGE,"E7.sketch_text.stroke-7"),sQuery(id+"F0.wireOp",EDGE,"E7.sketch_text.stroke-8"),sQuery(id+"F0.wireOp",EDGE,"E7.sketch_text.stroke-9"),sQuery(id+"F0.wireOp",EDGE,"E7.sketch_text.stroke-10"),sQuery(id+"F0.wireOp",EDGE,"E7.sketch_text.stroke-11")])]});
            var Q6;
            Q6=makeQuery(id+"F1.opExtrude","SWEPT_BODY",BODY,{"disambiguationData":[OSD([sQuery(id+"F0.wireOp",EDGE,"E8.sketch_text.stroke-0"),sQuery(id+"F0.wireOp",EDGE,"E8.sketch_text.stroke-1"),sQuery(id+"F0.wireOp",EDGE,"E8.sketch_text.stroke-2"),sQuery(id+"F0.wireOp",EDGE,"E8.sketch_text.stroke-3"),sQuery(id+"F0.wireOp",EDGE,"E8.sketch_text.stroke-4"),sQuery(id+"F0.wireOp",EDGE,"E8.sketch_text.stroke-5"),sQuery(id+"F0.wireOp",EDGE,"E8.sketch_text.stroke-6"),sQuery(id+"F0.wireOp",EDGE,"E8.sketch_text.stroke-7"),sQuery(id+"F0.wireOp",EDGE,"E8.sketch_text.stroke-8"),sQuery(id+"F0.wireOp",EDGE,"E8.sketch_text.stroke-9"),sQuery(id+"F0.wireOp",EDGE,"E8.sketch_text.stroke-10"),sQuery(id+"F0.wireOp",EDGE,"E8.sketch_text.stroke-11"),sQuery(id+"F0.wireOp",EDGE,"E8.sketch_text.stroke-12"),sQuery(id+"F0.wireOp",EDGE,"E8.sketch_text.stroke-13"),sQuery(id+"F0.wireOp",EDGE,"E8.sketch_text.stroke-14"),sQuery(id+"F0.wireOp",EDGE,"E8.sketch_text.stroke-15")])]});
            var Q7;
            Q7=makeQuery(id+"F1.opExtrude","SWEPT_BODY",BODY,{"disambiguationData":[OSD([sQuery(id+"F0.wireOp",EDGE,"E9")])]});
            var Q8;
            Q8=makeQuery(id+"F1.opExtrude","SWEPT_BODY",BODY,{"disambiguationData":[OSD([sQuery(id+"F0.wireOp",EDGE,"E10")])]});
            var Q9;
            Q9=makeQuery(id+"F1.opExtrude","SWEPT_BODY",BODY,{"disambiguationData":[OSD([sQuery(id+"F0.wireOp",EDGE,"E12.sketch_text.stroke-0"),sQuery(id+"F0.wireOp",EDGE,"E12.sketch_text.stroke-1"),sQuery(id+"F0.wireOp",EDGE,"E12.sketch_text.stroke-2"),sQuery(id+"F0.wireOp",EDGE,"E12.sketch_text.stroke-3"),sQuery(id+"F0.wireOp",EDGE,"E12.sketch_text.stroke-4"),sQuery(id+"F0.wireOp",EDGE,"E12.sketch_text.stroke-5"),sQuery(id+"F0.wireOp",EDGE,"E12.sketch_text.stroke-6"),sQuery(id+"F0.wireOp",EDGE,"E12.sketch_text.stroke-7"),sQuery(id+"F0.wireOp",EDGE,"E12.sketch_text.stroke-8"),sQuery(id+"F0.wireOp",EDGE,"E12.sketch_text.stroke-9"),sQuery(id+"F0.wireOp",EDGE,"E12.sketch_text.stroke-10"),sQuery(id+"F0.wireOp",EDGE,"E12.sketch_text.stroke-11")])]});
            var Q10;
            Q10=makeQuery(id+"F1.opExtrude","SWEPT_BODY",BODY,{"disambiguationData":[OSD([sQuery(id+"F0.wireOp",EDGE,"E13.sketch_text.stroke-0"),sQuery(id+"F0.wireOp",EDGE,"E13.sketch_text.stroke-1"),sQuery(id+"F0.wireOp",EDGE,"E13.sketch_text.stroke-2"),sQuery(id+"F0.wireOp",EDGE,"E13.sketch_text.stroke-3"),sQuery(id+"F0.wireOp",EDGE,"E13.sketch_text.stroke-4"),sQuery(id+"F0.wireOp",EDGE,"E13.sketch_text.stroke-5"),sQuery(id+"F0.wireOp",EDGE,"E13.sketch_text.stroke-6"),sQuery(id+"F0.wireOp",EDGE,"E13.sketch_text.stroke-7"),sQuery(id+"F0.wireOp",EDGE,"E13.sketch_text.stroke-8"),sQuery(id+"F0.wireOp",EDGE,"E13.sketch_text.stroke-9"),sQuery(id+"F0.wireOp",EDGE,"E13.sketch_text.stroke-10"),sQuery(id+"F0.wireOp",EDGE,"E13.sketch_text.stroke-11"),sQuery(id+"F0.wireOp",EDGE,"E13.sketch_text.stroke-12"),sQuery(id+"F0.wireOp",EDGE,"E13.sketch_text.stroke-13"),sQuery(id+"F0.wireOp",EDGE,"E13.sketch_text.stroke-14"),sQuery(id+"F0.wireOp",EDGE,"E13.sketch_text.stroke-15")])]});
            var Q11;
            Q11=makeQuery(id+"F1.opExtrude","SWEPT_BODY",BODY,{"disambiguationData":[OSD([sQuery(id+"F0.wireOp",EDGE,"E14.sketch_text.stroke-0"),sQuery(id+"F0.wireOp",EDGE,"E14.sketch_text.stroke-1"),sQuery(id+"F0.wireOp",EDGE,"E14.sketch_text.stroke-2"),sQuery(id+"F0.wireOp",EDGE,"E14.sketch_text.stroke-3"),sQuery(id+"F0.wireOp",EDGE,"E14.sketch_text.stroke-4"),sQuery(id+"F0.wireOp",EDGE,"E14.sketch_text.stroke-5"),sQuery(id+"F0.wireOp",EDGE,"E14.sketch_text.stroke-6"),sQuery(id+"F0.wireOp",EDGE,"E14.sketch_text.stroke-7"),sQuery(id+"F0.wireOp",EDGE,"E14.sketch_text.stroke-8"),sQuery(id+"F0.wireOp",EDGE,"E14.sketch_text.stroke-9"),sQuery(id+"F0.wireOp",EDGE,"E14.sketch_text.stroke-10"),sQuery(id+"F0.wireOp",EDGE,"E14.sketch_text.stroke-11"),sQuery(id+"F0.wireOp",EDGE,"E14.sketch_text.stroke-12"),sQuery(id+"F0.wireOp",EDGE,"E14.sketch_text.stroke-13"),sQuery(id+"F0.wireOp",EDGE,"E14.sketch_text.stroke-14"),sQuery(id+"F0.wireOp",EDGE,"E14.sketch_text.stroke-15"),sQuery(id+"F0.wireOp",EDGE,"E14.sketch_text.stroke-16"),sQuery(id+"F0.wireOp",EDGE,"E14.sketch_text.stroke-17")])]});
            var Q12;
            Q12=makeQuery(id+"F1.opExtrude","SWEPT_BODY",BODY,{"disambiguationData":[OSD([sQuery(id+"F0.wireOp",EDGE,"E15.sketch_text.stroke-0"),sQuery(id+"F0.wireOp",EDGE,"E15.sketch_text.stroke-1"),sQuery(id+"F0.wireOp",EDGE,"E15.sketch_text.stroke-2"),sQuery(id+"F0.wireOp",EDGE,"E15.sketch_text.stroke-3"),sQuery(id+"F0.wireOp",EDGE,"E15.sketch_text.stroke-4"),sQuery(id+"F0.wireOp",EDGE,"E15.sketch_text.stroke-5"),sQuery(id+"F0.wireOp",EDGE,"E15.sketch_text.stroke-6"),sQuery(id+"F0.wireOp",EDGE,"E15.sketch_text.stroke-7"),sQuery(id+"F0.wireOp",EDGE,"E15.sketch_text.stroke-8"),sQuery(id+"F0.wireOp",EDGE,"E15.sketch_text.stroke-9"),sQuery(id+"F0.wireOp",EDGE,"E15.sketch_text.stroke-10"),sQuery(id+"F0.wireOp",EDGE,"E15.sketch_text.stroke-11"),sQuery(id+"F0.wireOp",EDGE,"E15.sketch_text.stroke-12"),sQuery(id+"F0.wireOp",EDGE,"E15.sketch_text.stroke-13"),sQuery(id+"F0.wireOp",EDGE,"E15.sketch_text.stroke-14"),sQuery(id+"F0.wireOp",EDGE,"E15.sketch_text.stroke-15"),sQuery(id+"F0.wireOp",EDGE,"E15.sketch_text.stroke-16"),sQuery(id+"F0.wireOp",EDGE,"E15.sketch_text.stroke-17"),sQuery(id+"F0.wireOp",EDGE,"E15.sketch_text.stroke-18"),sQuery(id+"F0.wireOp",EDGE,"E15.sketch_text.stroke-19"),sQuery(id+"F0.wireOp",EDGE,"E15.sketch_text.stroke-20"),sQuery(id+"F0.wireOp",EDGE,"E15.sketch_text.stroke-21"),sQuery(id+"F0.wireOp",EDGE,"E15.sketch_text.stroke-22"),sQuery(id+"F0.wireOp",EDGE,"E15.sketch_text.stroke-23"),sQuery(id+"F0.wireOp",EDGE,"E15.sketch_text.stroke-24")])]});
            var Q13;
            Q13=makeQuery(id+"F1.opExtrude","SWEPT_BODY",BODY,{"disambiguationData":[OSD([sQuery(id+"F0.wireOp",EDGE,"E16.sketch_text.stroke-0"),sQuery(id+"F0.wireOp",EDGE,"E16.sketch_text.stroke-1"),sQuery(id+"F0.wireOp",EDGE,"E16.sketch_text.stroke-2"),sQuery(id+"F0.wireOp",EDGE,"E16.sketch_text.stroke-3"),sQuery(id+"F0.wireOp",EDGE,"E16.sketch_text.stroke-4"),sQuery(id+"F0.wireOp",EDGE,"E16.sketch_text.stroke-5"),sQuery(id+"F0.wireOp",EDGE,"E16.sketch_text.stroke-6"),sQuery(id+"F0.wireOp",EDGE,"E16.sketch_text.stroke-7"),sQuery(id+"F0.wireOp",EDGE,"E16.sketch_text.stroke-8"),sQuery(id+"F0.wireOp",EDGE,"E16.sketch_text.stroke-9"),sQuery(id+"F0.wireOp",EDGE,"E16.sketch_text.stroke-10"),sQuery(id+"F0.wireOp",EDGE,"E16.sketch_text.stroke-11"),sQuery(id+"F0.wireOp",EDGE,"E16.sketch_text.stroke-12"),sQuery(id+"F0.wireOp",EDGE,"E16.sketch_text.stroke-13"),sQuery(id+"F0.wireOp",EDGE,"E16.sketch_text.stroke-14")])]});
            var Q14;
            Q14=makeQuery(id+"F1.opExtrude","SWEPT_BODY",BODY,{"disambiguationData":[OSD([sQuery(id+"F0.wireOp",EDGE,"E17.sketch_text.stroke-0"),sQuery(id+"F0.wireOp",EDGE,"E17.sketch_text.stroke-1"),sQuery(id+"F0.wireOp",EDGE,"E17.sketch_text.stroke-2"),sQuery(id+"F0.wireOp",EDGE,"E17.sketch_text.stroke-3"),sQuery(id+"F0.wireOp",EDGE,"E17.sketch_text.stroke-4"),sQuery(id+"F0.wireOp",EDGE,"E17.sketch_text.stroke-5"),sQuery(id+"F0.wireOp",EDGE,"E17.sketch_text.stroke-6"),sQuery(id+"F0.wireOp",EDGE,"E17.sketch_text.stroke-7"),sQuery(id+"F0.wireOp",EDGE,"E17.sketch_text.stroke-8"),sQuery(id+"F0.wireOp",EDGE,"E17.sketch_text.stroke-9"),sQuery(id+"F0.wireOp",EDGE,"E17.sketch_text.stroke-10"),sQuery(id+"F0.wireOp",EDGE,"E17.sketch_text.stroke-11"),sQuery(id+"F0.wireOp",EDGE,"E17.sketch_text.stroke-12"),sQuery(id+"F0.wireOp",EDGE,"E17.sketch_text.stroke-13"),sQuery(id+"F0.wireOp",EDGE,"E17.sketch_text.stroke-14"),sQuery(id+"F0.wireOp",EDGE,"E17.sketch_text.stroke-15")])]});
            var Q15;
            Q15=makeQuery(id+"F1.opExtrude","SWEPT_BODY",BODY,{"disambiguationData":[OSD([sQuery(id+"F0.wireOp",EDGE,"E18.sketch_text.stroke-0"),sQuery(id+"F0.wireOp",EDGE,"E18.sketch_text.stroke-1"),sQuery(id+"F0.wireOp",EDGE,"E18.sketch_text.stroke-2"),sQuery(id+"F0.wireOp",EDGE,"E18.sketch_text.stroke-3"),sQuery(id+"F0.wireOp",EDGE,"E18.sketch_text.stroke-4"),sQuery(id+"F0.wireOp",EDGE,"E18.sketch_text.stroke-5"),sQuery(id+"F0.wireOp",EDGE,"E18.sketch_text.stroke-6"),sQuery(id+"F0.wireOp",EDGE,"E18.sketch_text.stroke-7"),sQuery(id+"F0.wireOp",EDGE,"E18.sketch_text.stroke-8"),sQuery(id+"F0.wireOp",EDGE,"E18.sketch_text.stroke-9"),sQuery(id+"F0.wireOp",EDGE,"E18.sketch_text.stroke-10"),sQuery(id+"F0.wireOp",EDGE,"E18.sketch_text.stroke-11"),sQuery(id+"F0.wireOp",EDGE,"E18.sketch_text.stroke-12"),sQuery(id+"F0.wireOp",EDGE,"E18.sketch_text.stroke-13"),sQuery(id+"F0.wireOp",EDGE,"E18.sketch_text.stroke-14"),sQuery(id+"F0.wireOp",EDGE,"E18.sketch_text.stroke-15")])]});
            var Q16;
            Q16=makeQuery(id+"F1.opExtrude","SWEPT_BODY",BODY,{"disambiguationData":[OSD([sQuery(id+"F0.wireOp",EDGE,"E19.sketch_text.stroke-0"),sQuery(id+"F0.wireOp",EDGE,"E19.sketch_text.stroke-1"),sQuery(id+"F0.wireOp",EDGE,"E19.sketch_text.stroke-2"),sQuery(id+"F0.wireOp",EDGE,"E19.sketch_text.stroke-3"),sQuery(id+"F0.wireOp",EDGE,"E19.sketch_text.stroke-4"),sQuery(id+"F0.wireOp",EDGE,"E19.sketch_text.stroke-5")])]});
            var Q17;
            Q17=makeQuery(id+"F1.opExtrude","SWEPT_BODY",BODY,{"disambiguationData":[OSD([sQuery(id+"F0.wireOp",EDGE,"E20.sketch_text.stroke-0"),sQuery(id+"F0.wireOp",EDGE,"E20.sketch_text.stroke-1"),sQuery(id+"F0.wireOp",EDGE,"E20.sketch_text.stroke-2"),sQuery(id+"F0.wireOp",EDGE,"E20.sketch_text.stroke-3"),sQuery(id+"F0.wireOp",EDGE,"E20.sketch_text.stroke-4"),sQuery(id+"F0.wireOp",EDGE,"E20.sketch_text.stroke-5"),sQuery(id+"F0.wireOp",EDGE,"E20.sketch_text.stroke-6"),sQuery(id+"F0.wireOp",EDGE,"E20.sketch_text.stroke-7"),sQuery(id+"F0.wireOp",EDGE,"E20.sketch_text.stroke-8"),sQuery(id+"F0.wireOp",EDGE,"E20.sketch_text.stroke-9"),sQuery(id+"F0.wireOp",EDGE,"E20.sketch_text.stroke-10"),sQuery(id+"F0.wireOp",EDGE,"E20.sketch_text.stroke-11")])]});
            var Q18;
            Q18=makeQuery(id+"F4.opExtrude","SWEPT_BODY",BODY,{"disambiguationData":[OSD([sQuery(id+"F3.wireOp",EDGE,"E22"),sQuery(id+"F3.wireOp",EDGE,"E23")])]});
            var Q19;
            Q19=makeQuery(id+"F1.opExtrude","SWEPT_BODY",BODY,{"disambiguationData":[OSD([sQuery(id+"F0.wireOp",EDGE,"E21.sketch_text.stroke-0"),sQuery(id+"F0.wireOp",EDGE,"E21.sketch_text.stroke-1"),sQuery(id+"F0.wireOp",EDGE,"E21.sketch_text.stroke-2"),sQuery(id+"F0.wireOp",EDGE,"E21.sketch_text.stroke-3"),sQuery(id+"F0.wireOp",EDGE,"E21.sketch_text.stroke-4"),sQuery(id+"F0.wireOp",EDGE,"E21.sketch_text.stroke-5"),sQuery(id+"F0.wireOp",EDGE,"E21.sketch_text.stroke-6"),sQuery(id+"F0.wireOp",EDGE,"E21.sketch_text.stroke-7"),sQuery(id+"F0.wireOp",EDGE,"E21.sketch_text.stroke-8"),sQuery(id+"F0.wireOp",EDGE,"E21.sketch_text.stroke-9"),sQuery(id+"F0.wireOp",EDGE,"E21.sketch_text.stroke-10"),sQuery(id+"F0.wireOp",EDGE,"E21.sketch_text.stroke-11")])]});
            booleanBodies(context, id + "F5", {"operationType" : BooleanOperationType.UNION, "tools" : qUnion([Q0, Q1, Q2, Q3, Q4, Q5, Q6, Q7, Q8, Q9, Q10, Q11, Q12, Q13, Q14, Q15, Q16, Q17, Q18, Q19])});
        }
        {
            var Q0;
            Q0=qCreatedBy(makeId("Top.planeOp"),FACE);
            var sketch = newSketch(context, id + "F6", { "sketchPlane" : qUnion([Q0])});
            skLineSegment(sketch, "E24.bottom", {"start": v(-20.22, 5.4) * mm, "end": v(20.22, 5.4) * mm});
            skLineSegment(sketch, "E24.top", {"start": v(-20.22, -5.4) * mm, "end": v(20.22, -5.4) * mm});
            skArc(sketch, "E25", {"start": v(-20.22, 5.4) * mm, "mid": v(-20.93, 0) * mm, "end": v(-20.22, -5.4) * mm});
            skArc(sketch, "E26", {"start": v(20.22, -5.4) * mm, "mid": v(20.93, 0) * mm, "end": v(20.22, 5.4) * mm});
            skLineSegment(sketch, "E27", {"start": v(20.22, 5.4) * mm, "end": v(20.22, -5.4) * mm, "construction": true});
            skLineSegment(sketch, "E28", {"start": v(-20.22, 5.4) * mm, "end": v(-20.22, -5.4) * mm, "construction": true});
            skCircle(sketch, "E29", {"center": v(0, 0) * mm, "radius": 20.93 * mm, "construction": true});
            skSolve(sketch);
        }
        {
            var Q0;
            Q0 = qSketchRegion(id + "F6", true);
            extrude(context, id + "F7", {"entities" : qUnion([Q0]), "operationType" : NewBodyOperationType.ADD, "oppositeDirection" : true, "depth" : 12.7 * mm, "offsetDistance" : 25.4 * mm});
        }
        {
            var Q0;
            {var subQ109=sQuery(id+"F0.wireOp",EDGE,"E2.sketch_text.stroke-0");var subQ157=sQuery(id+"F3.wireOp",EDGE,"E22");var subQ158=sQuery(id+"F3.wireOp",EDGE,"E23");Q0=makeQuery(id+"F7.boolean.opBoolean","MERGE",FACE,{"derivedFrom":[makeQuery(id+"F5.opBoolean","SPLIT",FACE,{"disambiguationData":[TD([makeQuery(id+"F1.opExtrude","SWEPT_FACE",FACE,{"disambiguationData":[OSD([subQ109])]})])],"derivedFrom":makeQuery(id+"F4.opExtrude","CAP_FACE",FACE,{"disambiguationData":[OSD([subQ157,subQ158])],"isStart":true})}),makeQuery(id+"F7.opExtrude","CAP_FACE",FACE,{"disambiguationData":[OSD([sQuery(id+"F6.wireOp",EDGE,"E24.bottom"),sQuery(id+"F6.wireOp",EDGE,"E24.top"),sQuery(id+"F6.wireOp",EDGE,"E25"),sQuery(id+"F6.wireOp",EDGE,"E26")])],"isStart":true})]});}
            var sketch = newSketch(context, id + "F8", { "sketchPlane" : qUnion([Q0])});
            skText(sketch, "E30", { "text": "Since 2002", "fontName": "OpenSans-Regular.ttf"});
            const initialGuessF8  = {"E30": [-0.00953, -0.00137, 1, 0, 0.00274]};
            skSetInitialGuess(sketch, initialGuessF8);
            skSolve(sketch);
        }
        {
            var Q0;
            Q0 = qSketchRegion(id + "F8", true);
            extrude(context, id + "F9", {"entities" : qUnion([Q0]), "operationType" : NewBodyOperationType.ADD, "depth" : 0.36 * mm, "offsetDistance" : 25.4 * mm});
        }
        {
            var Q0;
            Q0=makeQuery(id+"F9.opExtrude","CAP_FACE",FACE,{"disambiguationData":[OSD([sQuery(id+"F8.wireOp",EDGE,"E30.sketch_text.stroke-0"),sQuery(id+"F8.wireOp",EDGE,"E30.sketch_text.stroke-1"),sQuery(id+"F8.wireOp",EDGE,"E30.sketch_text.stroke-2"),sQuery(id+"F8.wireOp",EDGE,"E30.sketch_text.stroke-3"),sQuery(id+"F8.wireOp",EDGE,"E30.sketch_text.stroke-4"),sQuery(id+"F8.wireOp",EDGE,"E30.sketch_text.stroke-5"),sQuery(id+"F8.wireOp",EDGE,"E30.sketch_text.stroke-6"),sQuery(id+"F8.wireOp",EDGE,"E30.sketch_text.stroke-7"),sQuery(id+"F8.wireOp",EDGE,"E30.sketch_text.stroke-8"),sQuery(id+"F8.wireOp",EDGE,"E30.sketch_text.stroke-9"),sQuery(id+"F8.wireOp",EDGE,"E30.sketch_text.stroke-10"),sQuery(id+"F8.wireOp",EDGE,"E30.sketch_text.stroke-11"),sQuery(id+"F8.wireOp",EDGE,"E30.sketch_text.stroke-12"),sQuery(id+"F8.wireOp",EDGE,"E30.sketch_text.stroke-13"),sQuery(id+"F8.wireOp",EDGE,"E30.sketch_text.stroke-14"),sQuery(id+"F8.wireOp",EDGE,"E30.sketch_text.stroke-15"),sQuery(id+"F8.wireOp",EDGE,"E30.sketch_text.stroke-16"),sQuery(id+"F8.wireOp",EDGE,"E30.sketch_text.stroke-17"),sQuery(id+"F8.wireOp",EDGE,"E30.sketch_text.stroke-18"),sQuery(id+"F8.wireOp",EDGE,"E30.sketch_text.stroke-19"),sQuery(id+"F8.wireOp",EDGE,"E30.sketch_text.stroke-20"),sQuery(id+"F8.wireOp",EDGE,"E30.sketch_text.stroke-21"),sQuery(id+"F8.wireOp",EDGE,"E30.sketch_text.stroke-22"),sQuery(id+"F8.wireOp",EDGE,"E30.sketch_text.stroke-23"),sQuery(id+"F8.wireOp",EDGE,"E30.sketch_text.stroke-24")])],"isStart":false});
            var Q1;
            Q1=makeQuery(id+"F9.opExtrude","CAP_FACE",FACE,{"disambiguationData":[OSD([sQuery(id+"F8.wireOp",EDGE,"E30.sketch_text.stroke-25"),sQuery(id+"F8.wireOp",EDGE,"E30.sketch_text.stroke-26"),sQuery(id+"F8.wireOp",EDGE,"E30.sketch_text.stroke-27"),sQuery(id+"F8.wireOp",EDGE,"E30.sketch_text.stroke-28")])],"isStart":false});
            var Q2;
            Q2=makeQuery(id+"F9.opExtrude","CAP_FACE",FACE,{"disambiguationData":[OSD([sQuery(id+"F8.wireOp",EDGE,"E30.sketch_text.stroke-29"),sQuery(id+"F8.wireOp",EDGE,"E30.sketch_text.stroke-30"),sQuery(id+"F8.wireOp",EDGE,"E30.sketch_text.stroke-31"),sQuery(id+"F8.wireOp",EDGE,"E30.sketch_text.stroke-32"),sQuery(id+"F8.wireOp",EDGE,"E30.sketch_text.stroke-33"),sQuery(id+"F8.wireOp",EDGE,"E30.sketch_text.stroke-34"),sQuery(id+"F8.wireOp",EDGE,"E30.sketch_text.stroke-35"),sQuery(id+"F8.wireOp",EDGE,"E30.sketch_text.stroke-36")])],"isStart":false});
            var Q3;
            Q3=makeQuery(id+"F9.opExtrude","CAP_FACE",FACE,{"disambiguationData":[OSD([sQuery(id+"F8.wireOp",EDGE,"E30.sketch_text.stroke-37"),sQuery(id+"F8.wireOp",EDGE,"E30.sketch_text.stroke-38"),sQuery(id+"F8.wireOp",EDGE,"E30.sketch_text.stroke-39"),sQuery(id+"F8.wireOp",EDGE,"E30.sketch_text.stroke-40"),sQuery(id+"F8.wireOp",EDGE,"E30.sketch_text.stroke-41"),sQuery(id+"F8.wireOp",EDGE,"E30.sketch_text.stroke-42"),sQuery(id+"F8.wireOp",EDGE,"E30.sketch_text.stroke-43"),sQuery(id+"F8.wireOp",EDGE,"E30.sketch_text.stroke-44"),sQuery(id+"F8.wireOp",EDGE,"E30.sketch_text.stroke-45"),sQuery(id+"F8.wireOp",EDGE,"E30.sketch_text.stroke-46"),sQuery(id+"F8.wireOp",EDGE,"E30.sketch_text.stroke-47"),sQuery(id+"F8.wireOp",EDGE,"E30.sketch_text.stroke-48"),sQuery(id+"F8.wireOp",EDGE,"E30.sketch_text.stroke-49"),sQuery(id+"F8.wireOp",EDGE,"E30.sketch_text.stroke-50"),sQuery(id+"F8.wireOp",EDGE,"E30.sketch_text.stroke-51"),sQuery(id+"F8.wireOp",EDGE,"E30.sketch_text.stroke-52"),sQuery(id+"F8.wireOp",EDGE,"E30.sketch_text.stroke-53")])],"isStart":false});
            var Q4;
            Q4=makeQuery(id+"F9.opExtrude","CAP_FACE",FACE,{"disambiguationData":[OSD([sQuery(id+"F8.wireOp",EDGE,"E30.sketch_text.stroke-54"),sQuery(id+"F8.wireOp",EDGE,"E30.sketch_text.stroke-55"),sQuery(id+"F8.wireOp",EDGE,"E30.sketch_text.stroke-56"),sQuery(id+"F8.wireOp",EDGE,"E30.sketch_text.stroke-57"),sQuery(id+"F8.wireOp",EDGE,"E30.sketch_text.stroke-58"),sQuery(id+"F8.wireOp",EDGE,"E30.sketch_text.stroke-59"),sQuery(id+"F8.wireOp",EDGE,"E30.sketch_text.stroke-60"),sQuery(id+"F8.wireOp",EDGE,"E30.sketch_text.stroke-61"),sQuery(id+"F8.wireOp",EDGE,"E30.sketch_text.stroke-62"),sQuery(id+"F8.wireOp",EDGE,"E30.sketch_text.stroke-63"),sQuery(id+"F8.wireOp",EDGE,"E30.sketch_text.stroke-64"),sQuery(id+"F8.wireOp",EDGE,"E30.sketch_text.stroke-65"),sQuery(id+"F8.wireOp",EDGE,"E30.sketch_text.stroke-66"),sQuery(id+"F8.wireOp",EDGE,"E30.sketch_text.stroke-67"),sQuery(id+"F8.wireOp",EDGE,"E30.sketch_text.stroke-68")])],"isStart":false});
            var Q5;
            Q5=makeQuery(id+"F9.opExtrude","CAP_FACE",FACE,{"disambiguationData":[OSD([sQuery(id+"F8.wireOp",EDGE,"E30.sketch_text.stroke-69"),sQuery(id+"F8.wireOp",EDGE,"E30.sketch_text.stroke-70"),sQuery(id+"F8.wireOp",EDGE,"E30.sketch_text.stroke-71"),sQuery(id+"F8.wireOp",EDGE,"E30.sketch_text.stroke-72"),sQuery(id+"F8.wireOp",EDGE,"E30.sketch_text.stroke-73"),sQuery(id+"F8.wireOp",EDGE,"E30.sketch_text.stroke-74"),sQuery(id+"F8.wireOp",EDGE,"E30.sketch_text.stroke-75"),sQuery(id+"F8.wireOp",EDGE,"E30.sketch_text.stroke-76"),sQuery(id+"F8.wireOp",EDGE,"E30.sketch_text.stroke-77"),sQuery(id+"F8.wireOp",EDGE,"E30.sketch_text.stroke-78"),sQuery(id+"F8.wireOp",EDGE,"E30.sketch_text.stroke-79"),sQuery(id+"F8.wireOp",EDGE,"E30.sketch_text.stroke-80"),sQuery(id+"F8.wireOp",EDGE,"E30.sketch_text.stroke-81"),sQuery(id+"F8.wireOp",EDGE,"E30.sketch_text.stroke-82"),sQuery(id+"F8.wireOp",EDGE,"E30.sketch_text.stroke-83"),sQuery(id+"F8.wireOp",EDGE,"E30.sketch_text.stroke-84"),sQuery(id+"F8.wireOp",EDGE,"E30.sketch_text.stroke-85"),sQuery(id+"F8.wireOp",EDGE,"E30.sketch_text.stroke-86"),sQuery(id+"F8.wireOp",EDGE,"E30.sketch_text.stroke-87")])],"isStart":false});
            var Q6;
            Q6=makeQuery(id+"F9.opExtrude","CAP_FACE",FACE,{"disambiguationData":[OSD([sQuery(id+"F8.wireOp",EDGE,"E30.sketch_text.stroke-88"),sQuery(id+"F8.wireOp",EDGE,"E30.sketch_text.stroke-89"),sQuery(id+"F8.wireOp",EDGE,"E30.sketch_text.stroke-90"),sQuery(id+"F8.wireOp",EDGE,"E30.sketch_text.stroke-91"),sQuery(id+"F8.wireOp",EDGE,"E30.sketch_text.stroke-92"),sQuery(id+"F8.wireOp",EDGE,"E30.sketch_text.stroke-93"),sQuery(id+"F8.wireOp",EDGE,"E30.sketch_text.stroke-94"),sQuery(id+"F8.wireOp",EDGE,"E30.sketch_text.stroke-95"),sQuery(id+"F8.wireOp",EDGE,"E30.sketch_text.stroke-96"),sQuery(id+"F8.wireOp",EDGE,"E30.sketch_text.stroke-97"),sQuery(id+"F8.wireOp",EDGE,"E30.sketch_text.stroke-98"),sQuery(id+"F8.wireOp",EDGE,"E30.sketch_text.stroke-99"),sQuery(id+"F8.wireOp",EDGE,"E30.sketch_text.stroke-100"),sQuery(id+"F8.wireOp",EDGE,"E30.sketch_text.stroke-101"),sQuery(id+"F8.wireOp",EDGE,"E30.sketch_text.stroke-102"),sQuery(id+"F8.wireOp",EDGE,"E30.sketch_text.stroke-103"),sQuery(id+"F8.wireOp",EDGE,"E30.sketch_text.stroke-104"),sQuery(id+"F8.wireOp",EDGE,"E30.sketch_text.stroke-105"),sQuery(id+"F8.wireOp",EDGE,"E30.sketch_text.stroke-106"),sQuery(id+"F8.wireOp",EDGE,"E30.sketch_text.stroke-107")])],"isStart":false});
            var Q7;
            Q7=makeQuery(id+"F9.opExtrude","CAP_FACE",FACE,{"disambiguationData":[OSD([sQuery(id+"F8.wireOp",EDGE,"E30.sketch_text.stroke-108"),sQuery(id+"F8.wireOp",EDGE,"E30.sketch_text.stroke-109"),sQuery(id+"F8.wireOp",EDGE,"E30.sketch_text.stroke-110"),sQuery(id+"F8.wireOp",EDGE,"E30.sketch_text.stroke-111"),sQuery(id+"F8.wireOp",EDGE,"E30.sketch_text.stroke-112"),sQuery(id+"F8.wireOp",EDGE,"E30.sketch_text.stroke-113"),sQuery(id+"F8.wireOp",EDGE,"E30.sketch_text.stroke-114"),sQuery(id+"F8.wireOp",EDGE,"E30.sketch_text.stroke-115"),sQuery(id+"F8.wireOp",EDGE,"E30.sketch_text.stroke-116"),sQuery(id+"F8.wireOp",EDGE,"E30.sketch_text.stroke-117"),sQuery(id+"F8.wireOp",EDGE,"E30.sketch_text.stroke-118"),sQuery(id+"F8.wireOp",EDGE,"E30.sketch_text.stroke-119"),sQuery(id+"F8.wireOp",EDGE,"E30.sketch_text.stroke-120"),sQuery(id+"F8.wireOp",EDGE,"E30.sketch_text.stroke-121"),sQuery(id+"F8.wireOp",EDGE,"E30.sketch_text.stroke-122"),sQuery(id+"F8.wireOp",EDGE,"E30.sketch_text.stroke-123")])],"isStart":false});
            var Q8;
            Q8=makeQuery(id+"F9.opExtrude","CAP_FACE",FACE,{"disambiguationData":[OSD([sQuery(id+"F8.wireOp",EDGE,"E30.sketch_text.stroke-124"),sQuery(id+"F8.wireOp",EDGE,"E30.sketch_text.stroke-125"),sQuery(id+"F8.wireOp",EDGE,"E30.sketch_text.stroke-126"),sQuery(id+"F8.wireOp",EDGE,"E30.sketch_text.stroke-127"),sQuery(id+"F8.wireOp",EDGE,"E30.sketch_text.stroke-128"),sQuery(id+"F8.wireOp",EDGE,"E30.sketch_text.stroke-129"),sQuery(id+"F8.wireOp",EDGE,"E30.sketch_text.stroke-130"),sQuery(id+"F8.wireOp",EDGE,"E30.sketch_text.stroke-131"),sQuery(id+"F8.wireOp",EDGE,"E30.sketch_text.stroke-132"),sQuery(id+"F8.wireOp",EDGE,"E30.sketch_text.stroke-133"),sQuery(id+"F8.wireOp",EDGE,"E30.sketch_text.stroke-134"),sQuery(id+"F8.wireOp",EDGE,"E30.sketch_text.stroke-135"),sQuery(id+"F8.wireOp",EDGE,"E30.sketch_text.stroke-136"),sQuery(id+"F8.wireOp",EDGE,"E30.sketch_text.stroke-137"),sQuery(id+"F8.wireOp",EDGE,"E30.sketch_text.stroke-138"),sQuery(id+"F8.wireOp",EDGE,"E30.sketch_text.stroke-139")])],"isStart":false});
            var Q9;
            Q9=makeQuery(id+"F9.opExtrude","CAP_FACE",FACE,{"disambiguationData":[OSD([sQuery(id+"F8.wireOp",EDGE,"E30.sketch_text.stroke-140"),sQuery(id+"F8.wireOp",EDGE,"E30.sketch_text.stroke-141"),sQuery(id+"F8.wireOp",EDGE,"E30.sketch_text.stroke-142"),sQuery(id+"F8.wireOp",EDGE,"E30.sketch_text.stroke-143"),sQuery(id+"F8.wireOp",EDGE,"E30.sketch_text.stroke-144"),sQuery(id+"F8.wireOp",EDGE,"E30.sketch_text.stroke-145"),sQuery(id+"F8.wireOp",EDGE,"E30.sketch_text.stroke-146"),sQuery(id+"F8.wireOp",EDGE,"E30.sketch_text.stroke-147"),sQuery(id+"F8.wireOp",EDGE,"E30.sketch_text.stroke-148"),sQuery(id+"F8.wireOp",EDGE,"E30.sketch_text.stroke-149"),sQuery(id+"F8.wireOp",EDGE,"E30.sketch_text.stroke-150"),sQuery(id+"F8.wireOp",EDGE,"E30.sketch_text.stroke-151"),sQuery(id+"F8.wireOp",EDGE,"E30.sketch_text.stroke-152"),sQuery(id+"F8.wireOp",EDGE,"E30.sketch_text.stroke-153"),sQuery(id+"F8.wireOp",EDGE,"E30.sketch_text.stroke-154"),sQuery(id+"F8.wireOp",EDGE,"E30.sketch_text.stroke-155"),sQuery(id+"F8.wireOp",EDGE,"E30.sketch_text.stroke-156"),sQuery(id+"F8.wireOp",EDGE,"E30.sketch_text.stroke-157"),sQuery(id+"F8.wireOp",EDGE,"E30.sketch_text.stroke-158"),sQuery(id+"F8.wireOp",EDGE,"E30.sketch_text.stroke-159")])],"isStart":false});
            fillet(context, id + "F10", {"entities" : qUnion([Q0, Q1, Q2, Q3, Q4, Q5, Q6, Q7, Q8, Q9]), "radius" : 0.12 * mm, "tangentPropagation" : true, "allowEdgeOverflow" : false});
        }
    });
